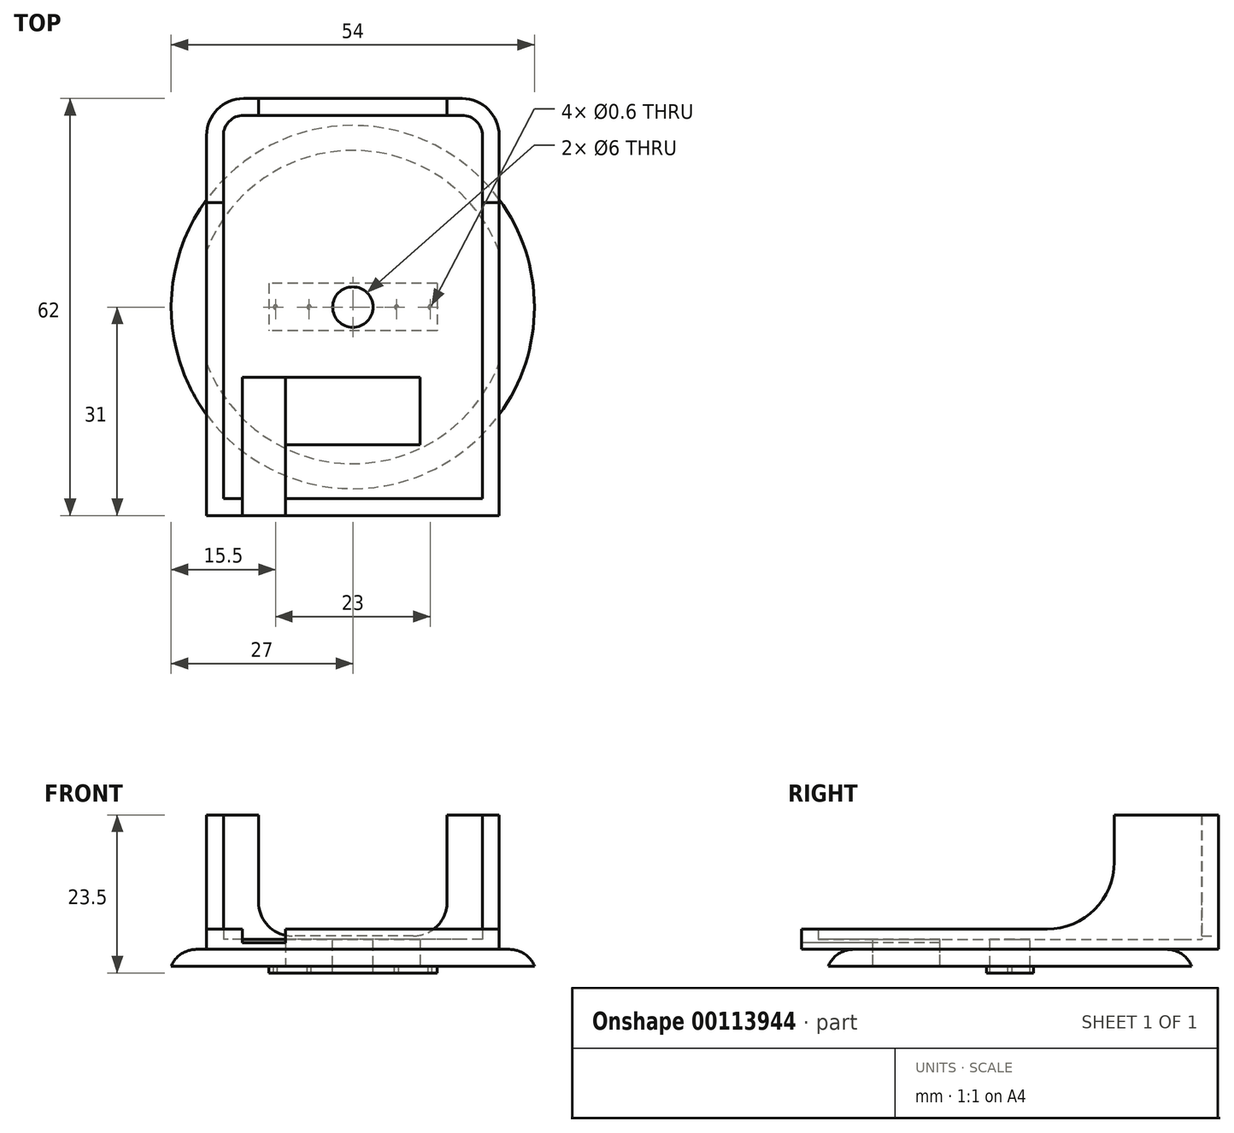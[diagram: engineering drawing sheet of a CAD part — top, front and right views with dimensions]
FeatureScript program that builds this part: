
annotation { "Feature Type Name" : "Feature", "Feature Type Description" : "" }
export const myFeature = defineFeature(function(context is Context, id is Id, definition is map)
    precondition{}
    {
        {
            var Q0;
            Q0=qCreatedBy(makeId("Top.planeOp"),FACE);
            var sketch = newSketch(context, id + "F0", { "sketchPlane" : qUnion([Q0])});
            skCircle(sketch, "E0", {"center": v(0, 0) * mm, "radius": 27 * mm});
            skCircle(sketch, "E1", {"center": v(0, 0) * mm, "radius": 3 * mm});
            skSolve(sketch);
        }
        {
            var Q0;
            Q0=makeQuery(id+"F0.imprint","IMPRINT",FACE,{"disambiguationData":[TD([[makeQuery(id+"F0.imprint","IMPRINT",EDGE,{"derivedFrom":sQuery(id+"F0.wireOp",EDGE,"E0")}),1.0]])]});
            extrude(context, id + "F1", {"entities" : qUnion([Q0]), "oppositeDirection" : true, "depth" : 2.5 * mm});
        }
        {
            var Q0;
            Q0=makeQuery(id+"F1.opExtrude","CAP_FACE",FACE,{"disambiguationData":[OSD([sQuery(id+"F0.wireOp",EDGE,"E0"),sQuery(id+"F0.wireOp",EDGE,"E1")])],"isStart":false});
            var sketch = newSketch(context, id + "F2", { "sketchPlane" : qUnion([Q0])});
            skLineSegment(sketch, "E2.bottom", {"start": v(12.5, -3.5) * mm, "end": v(-12.5, -3.5) * mm});
            skLineSegment(sketch, "E2.top", {"start": v(12.5, 3.5) * mm, "end": v(-12.5, 3.5) * mm});
            skLineSegment(sketch, "E2.left", {"start": v(12.5, -3.5) * mm, "end": v(12.5, 3.5) * mm});
            skLineSegment(sketch, "E2.right", {"start": v(-12.5, -3.5) * mm, "end": v(-12.5, 3.5) * mm});
            skPoint(sketch, "E2.middle", {"position": v(0, 0) * mm});
            skLineSegment(sketch, "E3", {"start": v(6.5, 0.3) * mm, "end": v(6.5, -0.3) * mm, "construction": true});
            skLineSegment(sketch, "E4", {"start": v(11.5, 0.3) * mm, "end": v(11.5, -0.3) * mm, "construction": true});
            skLineSegment(sketch, "E5", {"start": v(0, 3.5) * mm, "end": v(0, -3) * mm, "construction": true});
            skCircle(sketch, "E6", {"center": v(6.5, 0) * mm, "radius": 0.3 * mm});
            skCircle(sketch, "E7", {"center": v(11.5, 0) * mm, "radius": 0.3 * mm});
            skCircle(sketch, "E8.MirrorC", {"center": v(-6.5, 0) * mm, "radius": 0.3 * mm});
            skCircle(sketch, "E9.MirrorC", {"center": v(-11.5, 0) * mm, "radius": 0.3 * mm});
            skPoint(sketch, "E10.orphan", {"position": v(6.5, 3.5) * mm});
            skPoint(sketch, "E11.orphan", {"position": v(6.5, -3.5) * mm});
            skPoint(sketch, "E12.orphan", {"position": v(11.5, -3.5) * mm});
            skPoint(sketch, "E13.orphan", {"position": v(11.5, 3.5) * mm});
            skSolve(sketch);
        }
        {
            var Q0;
            Q0=makeQuery(id+"F2.imprint","IMPRINT",FACE,{"disambiguationData":[TD([[makeQuery(id+"F2.imprint","IMPRINT",EDGE,{"derivedFrom":sQuery(id+"F2.wireOp",EDGE,"E2.bottom")}),-1.0]])]});
            var Q1;
            Q1=sQuery(id+"F2.wireOp",EDGE,"E9.MirrorC");
            var Q2;
            Q2=sQuery(id+"F2.wireOp",EDGE,"E8.MirrorC");
            var Q3;
            Q3=sQuery(id+"F2.wireOp",EDGE,"E6");
            var Q4;
            Q4=sQuery(id+"F2.wireOp",EDGE,"E7");
            extrude(context, id + "F3", {"entities" : qUnion([Q0]), "surfaceEntities" : qUnion([Q1, Q2, Q3, Q4]), "depth" : 1 * mm});
        }
        {
            var Q0;
            Q0=makeQuery(id+"F1.opExtrude","CAP_EDGE",EDGE,{"disambiguationData":[OSD([sQuery(id+"F0.wireOp",EDGE,"E0")])],"isStart":true});
            fillet(context, id + "F4", {"entities" : qUnion([Q0]), "radius" : 4 * mm, "tangentPropagation" : true, "allowEdgeOverflow" : false});
        }
        {
            var Q0;
            Q0=makeQuery(id+"F1.opExtrude","CAP_FACE",FACE,{"disambiguationData":[OSD([sQuery(id+"F0.wireOp",EDGE,"E0"),sQuery(id+"F0.wireOp",EDGE,"E1")])],"isStart":true});
            var sketch = newSketch(context, id + "F5", { "sketchPlane" : qUnion([Q0])});
            skLineSegment(sketch, "E14.bottom", {"start": v(19.25, -28.5) * mm, "end": v(-19.25, -28.5) * mm});
            skLineSegment(sketch, "E14.top", {"start": v(16.25, 28.5) * mm, "end": v(-16.25, 28.5) * mm});
            skLineSegment(sketch, "E14.left", {"start": v(19.25, -28.5) * mm, "end": v(19.25, 25.5) * mm});
            skLineSegment(sketch, "E14.right", {"start": v(-19.25, -28.5) * mm, "end": v(-19.25, 25.5) * mm});
            skPoint(sketch, "E14.middle", {"position": v(0, 0) * mm});
            skLineSegment(sketch, "E15", {"start": v(0, 28.5) * mm, "end": v(0, -28.5) * mm, "construction": true});
            skLineSegment(sketch, "E16", {"start": v(-16.25, 22.5) * mm, "end": v(-16.25, 21.33) * mm, "construction": true});
            skArc(sketch, "E17", {"start": v(-16.25, 28.5) * mm, "mid": v(-18.37, 27.62) * mm, "end": v(-19.25, 25.5) * mm});
            skPoint(sketch, "E18.orphan", {"position": v(-19.25, 25.5) * mm});
            skPoint(sketch, "E19.orphan", {"position": v(-19.25, 28.5) * mm});
            skArc(sketch, "E20.MirrorCS", {"start": v(16.25, 28.5) * mm, "mid": v(18.37, 27.62) * mm, "end": v(19.25, 25.5) * mm});
            skPoint(sketch, "E21.orphan", {"position": v(19.25, 28.5) * mm});
            skArc(sketch, "E22.0", {"start": v(16.25, 31) * mm, "mid": v(20.14, 29.39) * mm, "end": v(21.75, 25.5) * mm});
            skArc(sketch, "E22.1", {"start": v(-16.25, 31) * mm, "mid": v(-20.14, 29.39) * mm, "end": v(-21.75, 25.5) * mm});
            skLineSegment(sketch, "E22.2", {"start": v(-21.75, -31) * mm, "end": v(-21.75, 25.5) * mm});
            skLineSegment(sketch, "E22.3", {"start": v(16.25, 31) * mm, "end": v(-16.25, 31) * mm});
            skLineSegment(sketch, "E22.4", {"start": v(21.75, -31) * mm, "end": v(-21.75, -31) * mm});
            skLineSegment(sketch, "E22.5", {"start": v(21.75, -31) * mm, "end": v(21.75, 25.5) * mm});
            skSolve(sketch);
        }
        {
            var Q0;
            {var subQ0=sQuery(id+"F5.wireOp",EDGE,"E14.bottom");Q0=makeQuery(id+"F5.imprint","IMPRINT",FACE,{"disambiguationData":[TD([[makeQuery(id+"F5.imprint","IMPRINT",EDGE,{"derivedFrom":subQ0}),-1.0]])]});}
            var Q1;
            {var subQ1=sQuery(id+"F0.wireOp",EDGE,"E1");Q1=makeQuery(id+"F5.imprint","IMPRINT",FACE,{"disambiguationData":[TD([[makeQuery(id+"F5.imprint","IMPRINT",EDGE,{"derivedFrom":makeQuery(id+"F1.opExtrude","CAP_EDGE",EDGE,{"disambiguationData":[OSD([subQ1])],"isStart":true})}),-1.0]])]});}
            var Q2;
            Q2=makeQuery(id+"F5.imprint","IMPRINT",FACE,{"disambiguationData":[TD([[makeQuery(id+"F5.imprint","IMPRINT",EDGE,{"derivedFrom":sQuery(id+"F5.wireOp",EDGE,"E14.top")}),1.0]])]});
            extrude(context, id + "F6", {"entities" : qUnion([Q0, Q1, Q2]), "operationType" : NewBodyOperationType.ADD, "depth" : 1.5 * mm});
        }
        {
            var Q0;
            Q0 = qSketchRegion(id + "F5", true);
            extrude(context, id + "F7", {"entities" : qUnion([Q0]), "operationType" : NewBodyOperationType.ADD, "depth" : 20 * mm});
        }
        {
            var Q0;
            Q0=makeQuery(id+"F7.opExtrude","SWEPT_FACE",FACE,{"disambiguationData":[OSD([sQuery(id+"F5.wireOp",EDGE,"E22.2")])]});
            var sketch = newSketch(context, id + "F8", { "sketchPlane" : qUnion([Q0])});
            skLineSegment(sketch, "E23", {"start": v(-15.5, 20) * mm, "end": v(-15.5, 0) * mm});
            skLineSegment(sketch, "E24", {"start": v(21, 20) * mm, "end": v(21, 0) * mm});
            skLineSegment(sketch, "E25", {"start": v(-25.5, 3) * mm, "end": v(31, 3) * mm});
            skSolve(sketch);
        }
        {
            var Q0;
            Q0 = qSketchRegion(id + "F8", true);
            var Q1;
            {var subQ0=sQuery(id+"F8.wireOp",EDGE,"E23");var subQ1=makeQuery(id+"F7.opExtrude","CAP_EDGE",EDGE,{"disambiguationData":[OSD([sQuery(id+"F5.wireOp",EDGE,"E22.2")])],"isStart":false});var subQ2=makeQuery(id+"F8.imprint","INTERSECT",VERTEX,{"derivedFrom":[subQ1,subQ0]});Q1=makeQuery(id+"F8.imprint","IMPRINT",FACE,{"disambiguationData":[TD([[makeQuery(id+"F8.imprint","IMPRINT",EDGE,{"disambiguationData":[TD([[subQ2,-1.0]])],"derivedFrom":subQ0}),1.0]])]});}
            var Q2;
            {var subQ0=sQuery(id+"F8.wireOp",EDGE,"E24");var subQ1=sQuery(id+"F5.wireOp",EDGE,"E22.2");var subQ2=makeQuery(id+"F7.opExtrude","CAP_EDGE",EDGE,{"disambiguationData":[OSD([subQ1])],"isStart":false});var subQ3=makeQuery(id+"F8.imprint","INTERSECT",VERTEX,{"derivedFrom":[subQ2,subQ0]});Q2=makeQuery(id+"F8.imprint","IMPRINT",FACE,{"disambiguationData":[TD([[makeQuery(id+"F8.imprint","IMPRINT",EDGE,{"disambiguationData":[TD([[subQ3,-1.0]])],"derivedFrom":subQ0}),1.0]])]});}
            extrude(context, id + "F9", {"entities" : qUnion([Q0, Q1, Q2]), "operationType" : NewBodyOperationType.REMOVE, "endBound" : BoundingType.THROUGH_ALL, "oppositeDirection" : true, "depth" : 25 * mm});
        }
        {
            var Q0;
            Q0=makeQuery(id+"F7.opExtrude","SWEPT_FACE",FACE,{"disambiguationData":[OSD([sQuery(id+"F5.wireOp",EDGE,"E22.3")])]});
            var sketch = newSketch(context, id + "F10", { "sketchPlane" : qUnion([Q0])});
            skLineSegment(sketch, "E26.top", {"start": v(14, 20.98) * mm, "end": v(-14, 20.98) * mm});
            skLineSegment(sketch, "E26.left", {"start": v(14, 2) * mm, "end": v(14, 20.98) * mm});
            skLineSegment(sketch, "E26.right", {"start": v(-14, 2) * mm, "end": v(-14, 20.98) * mm});
            skPoint(sketch, "E26.middle", {"position": v(0, 10.49) * mm});
            skPoint(sketch, "E26.middle.positionSnap0", {"position": v(0, 20) * mm});
            skPoint(sketch, "E26.centerSnap0", {"position": v(0, 20) * mm});
            skLineSegment(sketch, "E27", {"start": v(-14, 2) * mm, "end": v(14, 2) * mm});
            skPoint(sketch, "E28.orphan", {"position": v(-14, 0) * mm});
            skPoint(sketch, "E29.orphan", {"position": v(14, 0) * mm});
            skSolve(sketch);
        }
        {
            var Q0;
            {var subQ0=sQuery(id+"F10.wireOp",EDGE,"E27");Q0=makeQuery(id+"F10.imprint","IMPRINT",FACE,{"disambiguationData":[TD([[makeQuery(id+"F10.imprint","IMPRINT",EDGE,{"derivedFrom":subQ0}),1.0]])]});}
            extrude(context, id + "F11", {"entities" : qUnion([Q0]), "operationType" : NewBodyOperationType.REMOVE, "oppositeDirection" : true, "depth" : 2.5 * mm});
        }
        {
            var Q0;
            {var subQ0=sQuery(id+"F8.wireOp",EDGE,"E23");var subQ1=sQuery(id+"F8.wireOp",EDGE,"E25");Q0=makeQuery(id+"F9.boolean.opBoolean","COPY",EDGE,{"disambiguationData":[TD([makeQuery(id+"F7.opExtrude","SWEPT_FACE",FACE,{"disambiguationData":[OSD([sQuery(id+"F5.wireOp",EDGE,"E14.right")])]})])],"derivedFrom":makeQuery(id+"F9.opExtrude","SWEPT_EDGE",EDGE,{"disambiguationData":[OSD([subQ0,subQ1])]})});}
            var Q1;
            {var subQ0=sQuery(id+"F8.wireOp",EDGE,"E23");var subQ1=sQuery(id+"F8.wireOp",EDGE,"E25");Q1=makeQuery(id+"F9.boolean.opBoolean","COPY",EDGE,{"disambiguationData":[TD([makeQuery(id+"F7.opExtrude","SWEPT_FACE",FACE,{"disambiguationData":[OSD([sQuery(id+"F5.wireOp",EDGE,"E14.left")])]})])],"derivedFrom":makeQuery(id+"F9.opExtrude","SWEPT_EDGE",EDGE,{"disambiguationData":[OSD([subQ0,subQ1])]})});}
            fillet(context, id + "F12", {"entities" : qUnion([Q0, Q1]), "radius" : 10 * mm, "tangentPropagation" : true, "allowEdgeOverflow" : false});
        }
        {
            var Q0;
            Q0=makeQuery(id+"F11.boolean.opBoolean","COPY",EDGE,{"derivedFrom":makeQuery(id+"F11.opExtrude","SWEPT_EDGE",EDGE,{"disambiguationData":[OSD([sQuery(id+"F10.wireOp",EDGE,"E26.right"),sQuery(id+"F10.wireOp",EDGE,"E27")])]})});
            var Q1;
            Q1=makeQuery(id+"F11.boolean.opBoolean","COPY",EDGE,{"derivedFrom":makeQuery(id+"F11.opExtrude","SWEPT_EDGE",EDGE,{"disambiguationData":[OSD([sQuery(id+"F10.wireOp",EDGE,"E26.left"),sQuery(id+"F10.wireOp",EDGE,"E27")])]})});
            fillet(context, id + "F13", {"entities" : qUnion([Q0, Q1]), "radius" : 5 * mm, "tangentPropagation" : true, "allowEdgeOverflow" : false});
        }
        {
            var Q0;
            Q0=makeQuery(id+"F2.imprint","IMPRINT",FACE,{"disambiguationData":[TD([[makeQuery(id+"F2.imprint","IMPRINT",EDGE,{"derivedFrom":sQuery(id+"F2.wireOp",EDGE,"E2.bottom")}),1.0]])]});
            var sketch = newSketch(context, id + "F14", { "sketchPlane" : qUnion([Q0])});
            skLineSegment(sketch, "E30.bottom", {"start": v(10, 10.45) * mm, "end": v(-10, 10.45) * mm});
            skLineSegment(sketch, "E30.top", {"start": v(10, 20.45) * mm, "end": v(-10, 20.45) * mm});
            skLineSegment(sketch, "E30.left", {"start": v(10, 10.45) * mm, "end": v(10, 20.45) * mm});
            skLineSegment(sketch, "E30.right", {"start": v(-10, 10.45) * mm, "end": v(-10, 20.45) * mm});
            skPoint(sketch, "E30.middle", {"position": v(0, 15.45) * mm});
            skSolve(sketch);
        }
        {
            var Q0;
            Q0=makeQuery(id+"F14.imprint","IMPRINT",FACE,{"disambiguationData":[TD([[makeQuery(id+"F14.imprint","IMPRINT",EDGE,{"derivedFrom":sQuery(id+"F14.wireOp",EDGE,"E30.bottom")}),-1.0]])]});
            extrude(context, id + "F15", {"entities" : qUnion([Q0]), "operationType" : NewBodyOperationType.REMOVE, "oppositeDirection" : true, "depth" : 25 * mm});
        }
        {
            var Q0;
            Q0=makeQuery(id+"F9.boolean.opBoolean","COPY",FACE,{"derivedFrom":makeQuery(id+"F9.opExtrude","SWEPT_FACE",FACE,{"disambiguationData":[OSD([sQuery(id+"F8.wireOp",EDGE,"E25")])]})});
            var sketch = newSketch(context, id + "F16", { "sketchPlane" : qUnion([Q0])});
            skLineSegment(sketch, "E31.bottom", {"start": v(-9.98, -10.43) * mm, "end": v(-16.42, -10.43) * mm});
            skLineSegment(sketch, "E31.top", {"start": v(-9.98, -37.27) * mm, "end": v(-16.42, -37.27) * mm});
            skLineSegment(sketch, "E31.left", {"start": v(-9.98, -10.43) * mm, "end": v(-9.98, -37.27) * mm});
            skLineSegment(sketch, "E31.right", {"start": v(-16.42, -10.43) * mm, "end": v(-16.42, -37.27) * mm});
            skSolve(sketch);
        }
        {
            var Q0;
            Q0=makeQuery(id+"F16.imprint","IMPRINT",FACE,{"disambiguationData":[TD([[makeQuery(id+"F16.imprint","IMPRINT",EDGE,{"derivedFrom":sQuery(id+"F16.wireOp",EDGE,"E31.bottom")}),1.0]])]});
            var Q1;
            {var subQ0=sQuery(id+"F16.wireOp",EDGE,"E31.left");var subQ1=sQuery(id+"F8.wireOp",EDGE,"E25");var subQ2=makeQuery(id+"F9.boolean.opBoolean","INTERSECT",EDGE,{"derivedFrom":[makeQuery(id+"F7.opExtrude","SWEPT_FACE",FACE,{"disambiguationData":[OSD([sQuery(id+"F5.wireOp",EDGE,"E14.bottom")])]}),makeQuery(id+"F9.opExtrude","SWEPT_FACE",FACE,{"disambiguationData":[OSD([subQ1])]})]});var subQ3=makeQuery(id+"F16.imprint","INTERSECT",VERTEX,{"derivedFrom":[subQ2,subQ0]});Q1=makeQuery(id+"F16.imprint","IMPRINT",FACE,{"disambiguationData":[TD([[makeQuery(id+"F16.imprint","IMPRINT",EDGE,{"disambiguationData":[TD([[subQ3,-1.0]])],"derivedFrom":subQ0}),-1.0]])]});}
            extrude(context, id + "F17", {"entities" : qUnion([Q0, Q1]), "operationType" : NewBodyOperationType.REMOVE, "oppositeDirection" : true, "depth" : 2 * mm});
        }
    });
